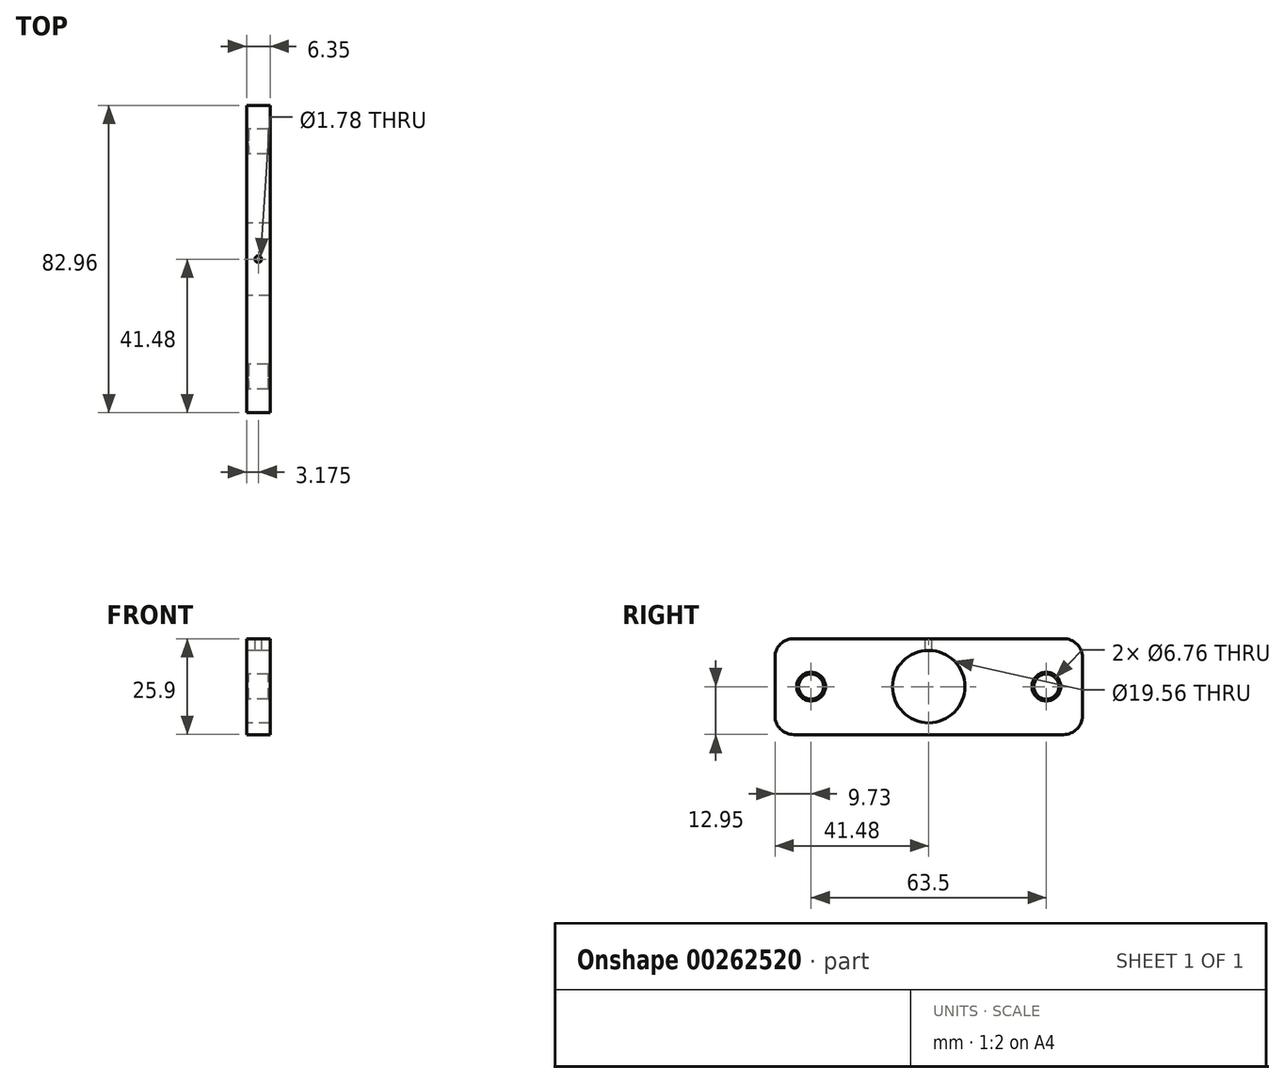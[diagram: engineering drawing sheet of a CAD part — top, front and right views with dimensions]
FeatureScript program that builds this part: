
annotation { "Feature Type Name" : "Feature", "Feature Type Description" : "" }
export const myFeature = defineFeature(function(context is Context, id is Id, definition is map)
    precondition{}
    {
        {
            var Q0;
            Q0=qCreatedBy(makeId("Right.planeOp"),FACE);
            var sketch = newSketch(context, id + "F0", { "sketchPlane" : qUnion([Q0])});
            skLineSegment(sketch, "E0.bottom", {"start": v(41.48, -12.95) * mm, "end": v(-41.48, -12.95) * mm});
            skLineSegment(sketch, "E0.top", {"start": v(41.48, 12.95) * mm, "end": v(-41.48, 12.95) * mm});
            skLineSegment(sketch, "E0.left", {"start": v(41.48, -12.95) * mm, "end": v(41.48, 12.95) * mm});
            skLineSegment(sketch, "E0.right", {"start": v(-41.48, -12.95) * mm, "end": v(-41.48, 12.95) * mm});
            skPoint(sketch, "E0.middle", {"position": v(0, 0) * mm});
            skCircle(sketch, "E1", {"center": v(-31.75, 0) * mm, "radius": 3.38 * mm});
            skCircle(sketch, "E2", {"center": v(31.75, 0) * mm, "radius": 3.38 * mm});
            skCircle(sketch, "E3", {"center": v(0, 0) * mm, "radius": 9.78 * mm});
            skSolve(sketch);
        }
        {
            var Q0;
            Q0 = qSketchRegion(id + "F0", true);
            extrude(context, id + "F1", {"entities" : qUnion([Q0]), "depth" : 6.35 * mm});
        }
        {
            var Q0;
            Q0=makeQuery(id+"F1.opExtrude","SWEPT_FACE",FACE,{"disambiguationData":[OSD([sQuery(id+"F0.wireOp",EDGE,"E0.top")])]});
            var sketch = newSketch(context, id + "F2", { "sketchPlane" : qUnion([Q0])});
            skCircle(sketch, "E4", {"center": v(3.18, 0) * mm, "radius": 0.89 * mm});
            skLineSegment(sketch, "E5", {"start": v(0, 0) * mm, "end": v(3.18, 0) * mm, "construction": true});
            skLineSegment(sketch, "E6", {"start": v(6.35, 0) * mm, "end": v(3.18, 0) * mm, "construction": true});
            skSolve(sketch);
        }
        {
            var Q0;
            Q0=makeQuery(id+"F1.opExtrude","SWEPT_EDGE",EDGE,{"disambiguationData":[OSD([sQuery(id+"F0.wireOp",EDGE,"E0.top"),sQuery(id+"F0.wireOp",EDGE,"E0.right")])]});
            var Q1;
            Q1=makeQuery(id+"F1.opExtrude","SWEPT_EDGE",EDGE,{"disambiguationData":[OSD([sQuery(id+"F0.wireOp",EDGE,"E0.top"),sQuery(id+"F0.wireOp",EDGE,"E0.left")])]});
            var Q2;
            Q2=makeQuery(id+"F1.opExtrude","SWEPT_EDGE",EDGE,{"disambiguationData":[OSD([sQuery(id+"F0.wireOp",EDGE,"E0.bottom"),sQuery(id+"F0.wireOp",EDGE,"E0.left")])]});
            var Q3;
            Q3=makeQuery(id+"F1.opExtrude","SWEPT_EDGE",EDGE,{"disambiguationData":[OSD([sQuery(id+"F0.wireOp",EDGE,"E0.bottom"),sQuery(id+"F0.wireOp",EDGE,"E0.right")])]});
            fillet(context, id + "F3", {"entities" : qUnion([Q0, Q1, Q2, Q3]), "radius" : 5.08 * mm, "tangentPropagation" : true, "allowEdgeOverflow" : false});
        }
        {
            var Q0;
            Q0=makeQuery(id+"F1.opExtrude","CAP_EDGE",EDGE,{"disambiguationData":[OSD([sQuery(id+"F0.wireOp",EDGE,"E2")])],"isStart":true});
            var Q1;
            Q1=makeQuery(id+"F1.opExtrude","CAP_EDGE",EDGE,{"disambiguationData":[OSD([sQuery(id+"F0.wireOp",EDGE,"E2")])],"isStart":false});
            var Q2;
            Q2=makeQuery(id+"F1.opExtrude","CAP_EDGE",EDGE,{"disambiguationData":[OSD([sQuery(id+"F0.wireOp",EDGE,"E1")])],"isStart":true});
            var Q3;
            Q3=makeQuery(id+"F1.opExtrude","CAP_EDGE",EDGE,{"disambiguationData":[OSD([sQuery(id+"F0.wireOp",EDGE,"E1")])],"isStart":false});
            chamfer(context, id + "F4", {"entities" : qUnion([Q0, Q1, Q2, Q3]), "width" : 0.5 * mm, "tangentPropagation" : true});
        }
        {
            var Q0;
            Q0 = qSketchRegion(id + "F2", true);
            extrude(context, id + "F5", {"entities" : qUnion([Q0]), "operationType" : NewBodyOperationType.REMOVE, "endBound" : BoundingType.UP_TO_NEXT, "oppositeDirection" : true, "depth" : 25.4 * mm});
        }
    });
